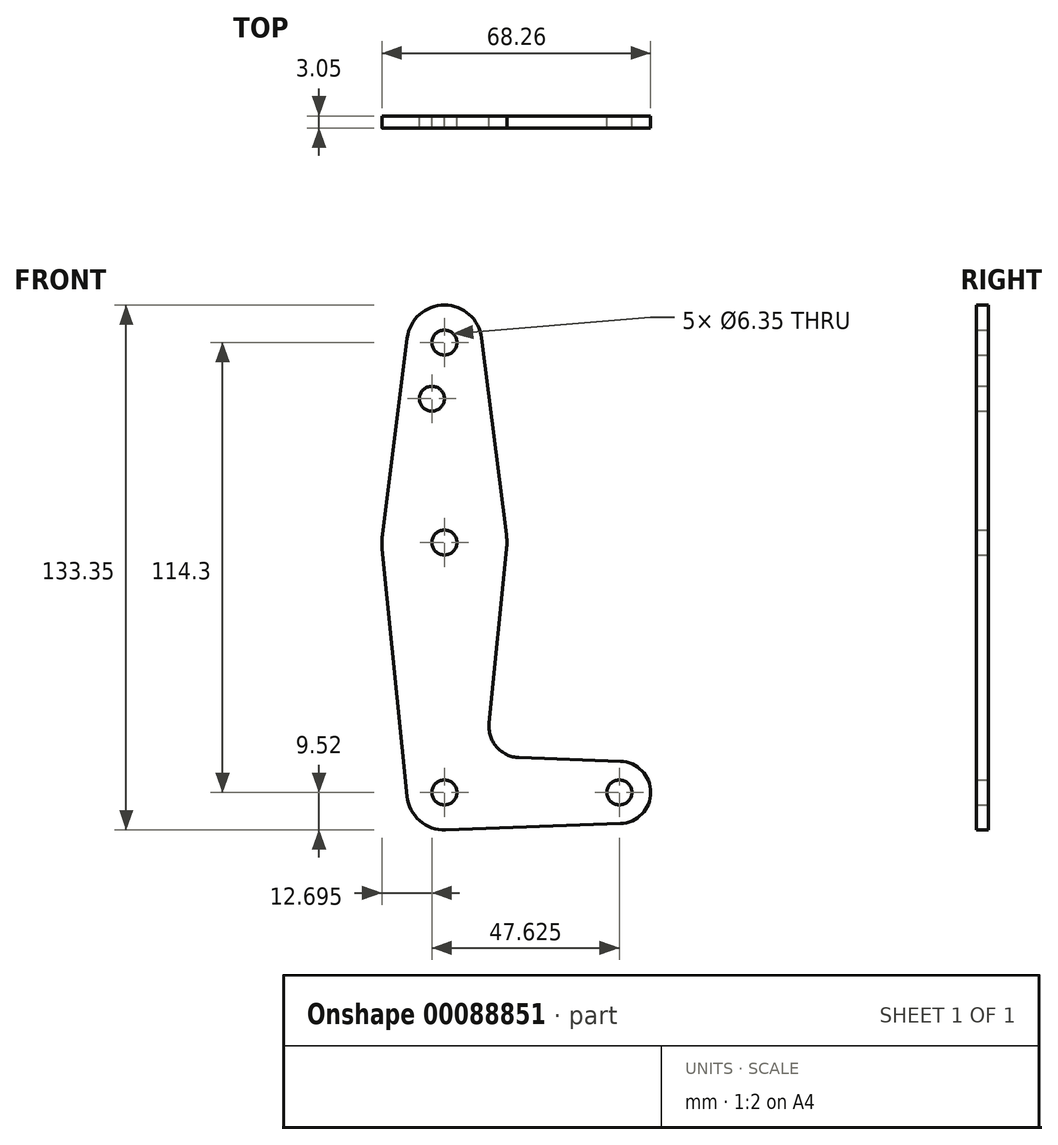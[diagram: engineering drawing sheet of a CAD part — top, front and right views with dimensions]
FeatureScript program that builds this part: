
annotation { "Feature Type Name" : "Feature", "Feature Type Description" : "" }
export const myFeature = defineFeature(function(context is Context, id is Id, definition is map)
    precondition{}
    {
        {
            var Q0;
            Q0=qCreatedBy(makeId("Front.planeOp"),FACE);
            var sketch = newSketch(context, id + "F0", { "sketchPlane" : qUnion([Q0])});
            skLineSegment(sketch, "E0", {"start": v(0, 114.3) * mm, "end": v(0, 0) * mm, "construction": true});
            skCircle(sketch, "E1", {"center": v(0, 114.3) * mm, "radius": 9.53 * mm});
            skCircle(sketch, "E2", {"center": v(0, 63.5) * mm, "radius": 15.88 * mm});
            skCircle(sketch, "E3", {"center": v(0, 0) * mm, "radius": 9.53 * mm});
            skLineSegment(sketch, "E4", {"start": v(0, 0) * mm, "end": v(44.45, 0) * mm, "construction": true});
            skCircle(sketch, "E5", {"center": v(44.45, 0) * mm, "radius": 7.94 * mm});
            skLineSegment(sketch, "E6", {"start": v(-9.45, 115.5) * mm, "end": v(-15.75, 65.48) * mm});
            skLineSegment(sketch, "E7", {"start": v(9.45, 115.5) * mm, "end": v(15.75, 65.48) * mm});
            skCircle(sketch, "E8", {"center": v(-3.18, 100.03) * mm, "radius": 3.18 * mm});
            skCircle(sketch, "E9", {"center": v(0, 63.5) * mm, "radius": 3.18 * mm});
            skCircle(sketch, "E10", {"center": v(0, 114.3) * mm, "radius": 3.18 * mm});
            skCircle(sketch, "E11", {"center": v(0, 0) * mm, "radius": 3.18 * mm});
            skCircle(sketch, "E12", {"center": v(44.45, 0) * mm, "radius": 3.18 * mm});
            skLineSegment(sketch, "E13", {"start": v(-15.8, 61.91) * mm, "end": v(-9.48, -0.95) * mm});
            skLineSegment(sketch, "E14", {"start": v(15.8, 61.91) * mm, "end": v(11.34, 17.6) * mm});
            skLineSegment(sketch, "E15", {"start": v(18.97, 8.85) * mm, "end": v(44.73, 7.93) * mm});
            skLineSegment(sketch, "E16", {"start": v(0.34, -9.52) * mm, "end": v(44.73, -7.93) * mm});
            skArc(sketch, "E17.filletArc", {"start": v(11.34, 17.6) * mm, "mid": v(13.26, 11.57) * mm, "end": v(18.97, 8.85) * mm});
            skSolve(sketch);
        }
        {
            var Q0;
            Q0 = qSketchRegion(id + "F0", true);
            extrude(context, id + "F1", {"entities" : qUnion([Q0]), "depth" : 3.05 * mm});
        }
    });
